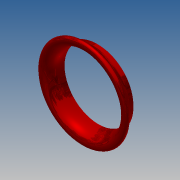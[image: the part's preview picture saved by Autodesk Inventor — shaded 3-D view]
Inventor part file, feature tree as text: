
AUTODESK INVENTOR PART (.ipt)
format: ipt  version: 2017.3 (Build 213257000, 257)  size: 257,024 bytes
history: native  units: in
note: dims shown in document units (in); Inventor stores cm internally (conversion verified against a paired STEP export)
features: sketch x4, extrude x3, fillet x2, revolve x1, chamfer x1, projected_geometry x1
ambient origin geometry x8: Origin, YZ Plane, XZ Plane, XY Plane, X Axis, Y Axis, Z Axis, Center Point
bodies: Solid1 (feature_tree)
feature tree (12):
  revolve  "Revolution1"  [1 undecoded]
  extrude  "Extrusion8"  Depth=9.5in
  fillet  "Fillet14"  [1 undecoded]
  extrude  "Extrusion10"  Depth=5.7in
  extrude  "Extrusion9"  Depth=0.751in
  fillet  "Fillet15"  Radius=2.052in
  chamfer  "Chamfer4"  Distance=0.265in
  sketch  "Sketch1"  dims[d1=30.75in d3=28.5in]
  sketch  "Sketch9"  dims[d4=28.5in d5=9.5in d6=15.0deg]
  sketch  "Sketch10"  dims[d7=5.7in d8=0.1412in]
  sketch  "Sketch11"  dims[d9=3.42in d10=0.1935in d11=2.052in d12=0.265in d13=1.2312in d14=0.3631in d17=0.7387in d18=0.5497in d19=3.0in d20=90.0deg d37=0.0in d94=37.8796in d95=30.516in d96=1.375in d97=0.0in d98=0.0312in d99=6.3386in d100=0.751in d101=35.2368in d103=0.5in d104=0.0in d105=0.0312in d106=0.0312in d107=0.125in d108=45.0deg d109=0.25in d110=0.0in d111=0.49in d112=0.751in]
  projected_geometry  "Projected Loop1"
note: 2 required parameter values undecoded (feature->parameter linkage not recoverable at this tier; creation-order binding heuristic only, values carry confidence <= 0.55)